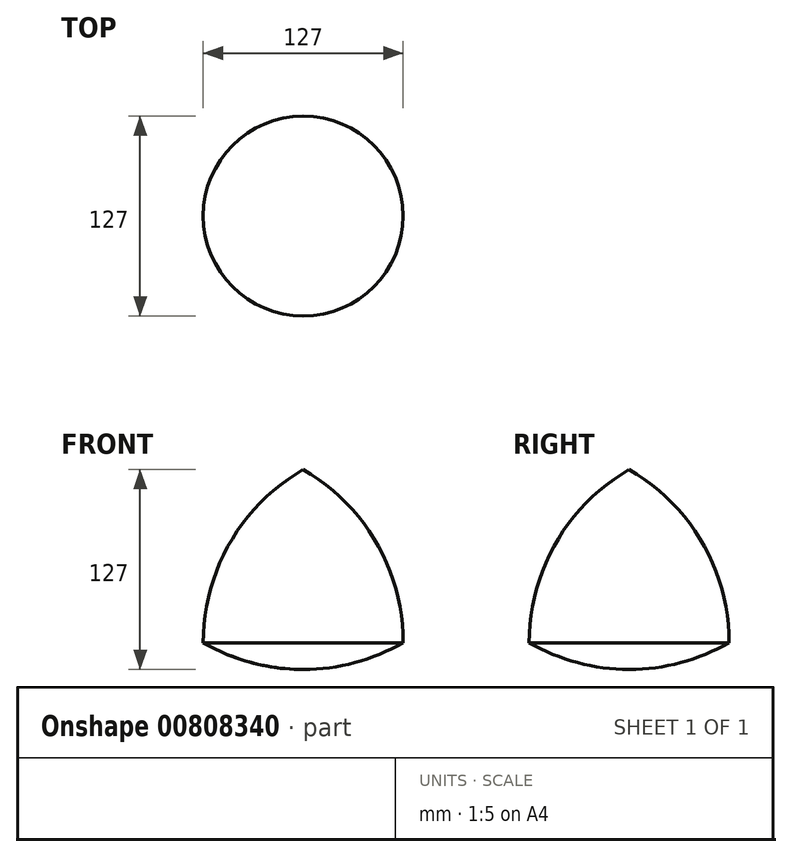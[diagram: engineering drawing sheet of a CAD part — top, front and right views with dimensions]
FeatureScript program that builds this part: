
annotation { "Feature Type Name" : "Feature", "Feature Type Description" : "" }
export const myFeature = defineFeature(function(context is Context, id is Id, definition is map)
    precondition{}
    {
        {
            var Q0;
            Q0=qCreatedBy(makeId("Front.planeOp"),FACE);
            var sketch = newSketch(context, id + "F0", { "sketchPlane" : qUnion([Q0])});
            skLineSegment(sketch, "E0", {"start": v(0, 0) * mm, "end": v(-63.5, 109.99) * mm});
            skLineSegment(sketch, "E1", {"start": v(-63.5, 109.99) * mm, "end": v(-127, 0) * mm});
            skLineSegment(sketch, "E2", {"start": v(-127, 0) * mm, "end": v(0, 0) * mm});
            skArc(sketch, "E3", {"start": v(0, 0) * mm, "mid": v(-17.01, 63.5) * mm, "end": v(-63.5, 109.99) * mm});
            skArc(sketch, "E4", {"start": v(-127, 0) * mm, "mid": v(-63.5, -17.01) * mm, "end": v(0, 0) * mm});
            skArc(sketch, "E5", {"start": v(-63.5, 109.99) * mm, "mid": v(-109.99, 63.5) * mm, "end": v(-127, 0) * mm});
            skLineSegment(sketch, "E6", {"start": v(-63.5, 109.99) * mm, "end": v(-63.5, -17.01) * mm});
            skSolve(sketch);
        }
        {
            var Q0;
            {var subQ0=sQuery(id+"F0.wireOp",EDGE,"E1");Q0=makeQuery(id+"F0.imprint","IMPRINT",FACE,{"disambiguationData":[TD([[makeQuery(id+"F0.imprint","IMPRINT",EDGE,{"derivedFrom":subQ0}),1.0]])]});}
            var Q1;
            Q1=makeQuery(id+"F0.imprint","IMPRINT",FACE,{"disambiguationData":[TD([[makeQuery(id+"F0.imprint","IMPRINT",EDGE,{"derivedFrom":sQuery(id+"F0.wireOp",EDGE,"E1")}),-1.0]])]});
            var Q2;
            {var subQ0=sQuery(id+"F0.wireOp",EDGE,"E4");var subQ3=sQuery(id+"F0.wireOp",EDGE,"E6");var subQ5=makeQuery(id+"F0.imprint","INTERSECT",VERTEX,{"derivedFrom":[subQ0,subQ3]});Q2=makeQuery(id+"F0.imprint","IMPRINT",FACE,{"disambiguationData":[TD([[makeQuery(id+"F0.imprint","IMPRINT",EDGE,{"disambiguationData":[TD([[subQ5,1.0]])],"derivedFrom":subQ3}),-1.0]])]});}
            var Q3;
            Q3=sQuery(id+"F0.wireOp",EDGE,"E6");
            revolve(context, id + "F1", {"surfaceOperationType" : NewSurfaceOperationType.NEW, "entities" : qUnion([Q0, Q1, Q2]), "axis" : qUnion([Q3]), "revolveType" : RevolveType.FULL});
        }
    });
